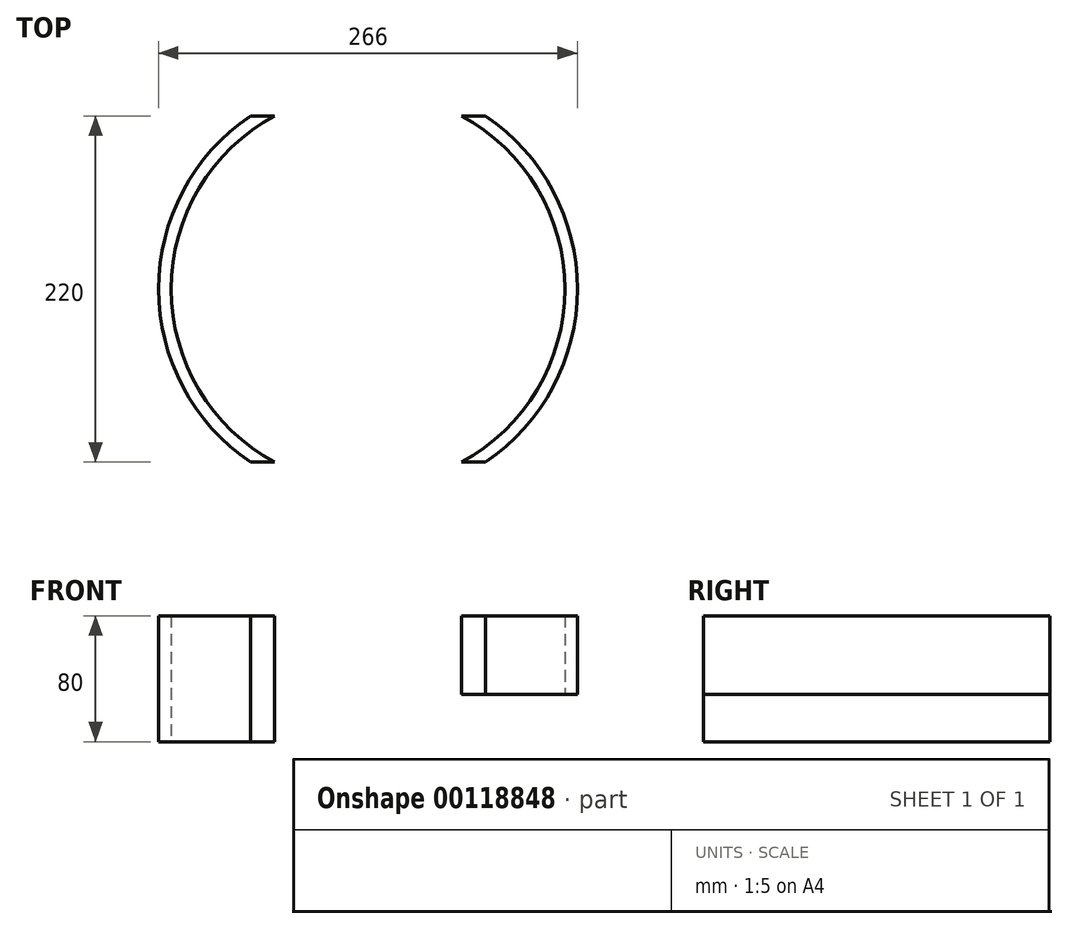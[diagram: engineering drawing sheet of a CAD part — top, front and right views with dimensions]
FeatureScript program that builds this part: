
annotation { "Feature Type Name" : "Feature", "Feature Type Description" : "" }
export const myFeature = defineFeature(function(context is Context, id is Id, definition is map)
    precondition{}
    {
        {
            var Q0;
            Q0=qCreatedBy(makeId("Top.planeOp"),FACE);
            var sketch = newSketch(context, id + "F0", { "sketchPlane" : qUnion([Q0])});
            skArc(sketch, "E0", {"start": v(-139.33, 110) * mm, "mid": v(-204.96, 0) * mm, "end": v(-139.33, -110) * mm});
            skArc(sketch, "E1", {"start": v(-20.59, -110) * mm, "mid": v(45.04, 0) * mm, "end": v(-20.59, 110) * mm});
            skLineSegment(sketch, "E2", {"start": v(-139.33, 110) * mm, "end": v(-20.59, 110) * mm});
            skLineSegment(sketch, "E3", {"start": v(-139.33, -110) * mm, "end": v(-20.59, -110) * mm});
            skLineSegment(sketch, "E4", {"start": v(-139.33, 110) * mm, "end": v(-154.72, 110) * mm});
            skLineSegment(sketch, "E5", {"start": v(-20.59, 110) * mm, "end": v(-5.2, 110) * mm});
            skLineSegment(sketch, "E6", {"start": v(-139.33, -110) * mm, "end": v(-154.72, -110) * mm});
            skLineSegment(sketch, "E7", {"start": v(-20.59, -110) * mm, "end": v(-5.2, -110) * mm});
            skArc(sketch, "E8", {"start": v(-154.72, 110) * mm, "mid": v(-212.96, 0) * mm, "end": v(-154.72, -110) * mm});
            skArc(sketch, "E9", {"start": v(-5.2, -110) * mm, "mid": v(53.04, 0) * mm, "end": v(-5.2, 110) * mm});
            skSolve(sketch);
        }
        {
            var Q0;
            Q0=makeQuery(id+"F0.imprint","IMPRINT",FACE,{"disambiguationData":[TD([[makeQuery(id+"F0.imprint","IMPRINT",EDGE,{"derivedFrom":sQuery(id+"F0.wireOp",EDGE,"E0")}),-1.0]])]});
            var Q1;
            Q1=makeQuery(id+"F0.imprint","IMPRINT",FACE,{"disambiguationData":[TD([[makeQuery(id+"F0.imprint","IMPRINT",EDGE,{"derivedFrom":sQuery(id+"F0.wireOp",EDGE,"E1")}),-1.0]])]});
            extrude(context, id + "F1", {"entities" : qUnion([Q0, Q1]), "depth" : 80 * mm});
        }
        {
            var Q0;
            Q0=makeQuery(id+"F1.opExtrude","CAP_FACE",FACE,{"disambiguationData":[OSD([sQuery(id+"F0.wireOp",EDGE,"E1"),sQuery(id+"F0.wireOp",EDGE,"E5"),sQuery(id+"F0.wireOp",EDGE,"E7"),sQuery(id+"F0.wireOp",EDGE,"E9")])],"isStart":true});
            extrude(context, id + "F2", {"entities" : qUnion([Q0]), "operationType" : NewBodyOperationType.REMOVE, "oppositeDirection" : true, "depth" : 30 * mm});
        }
    });
